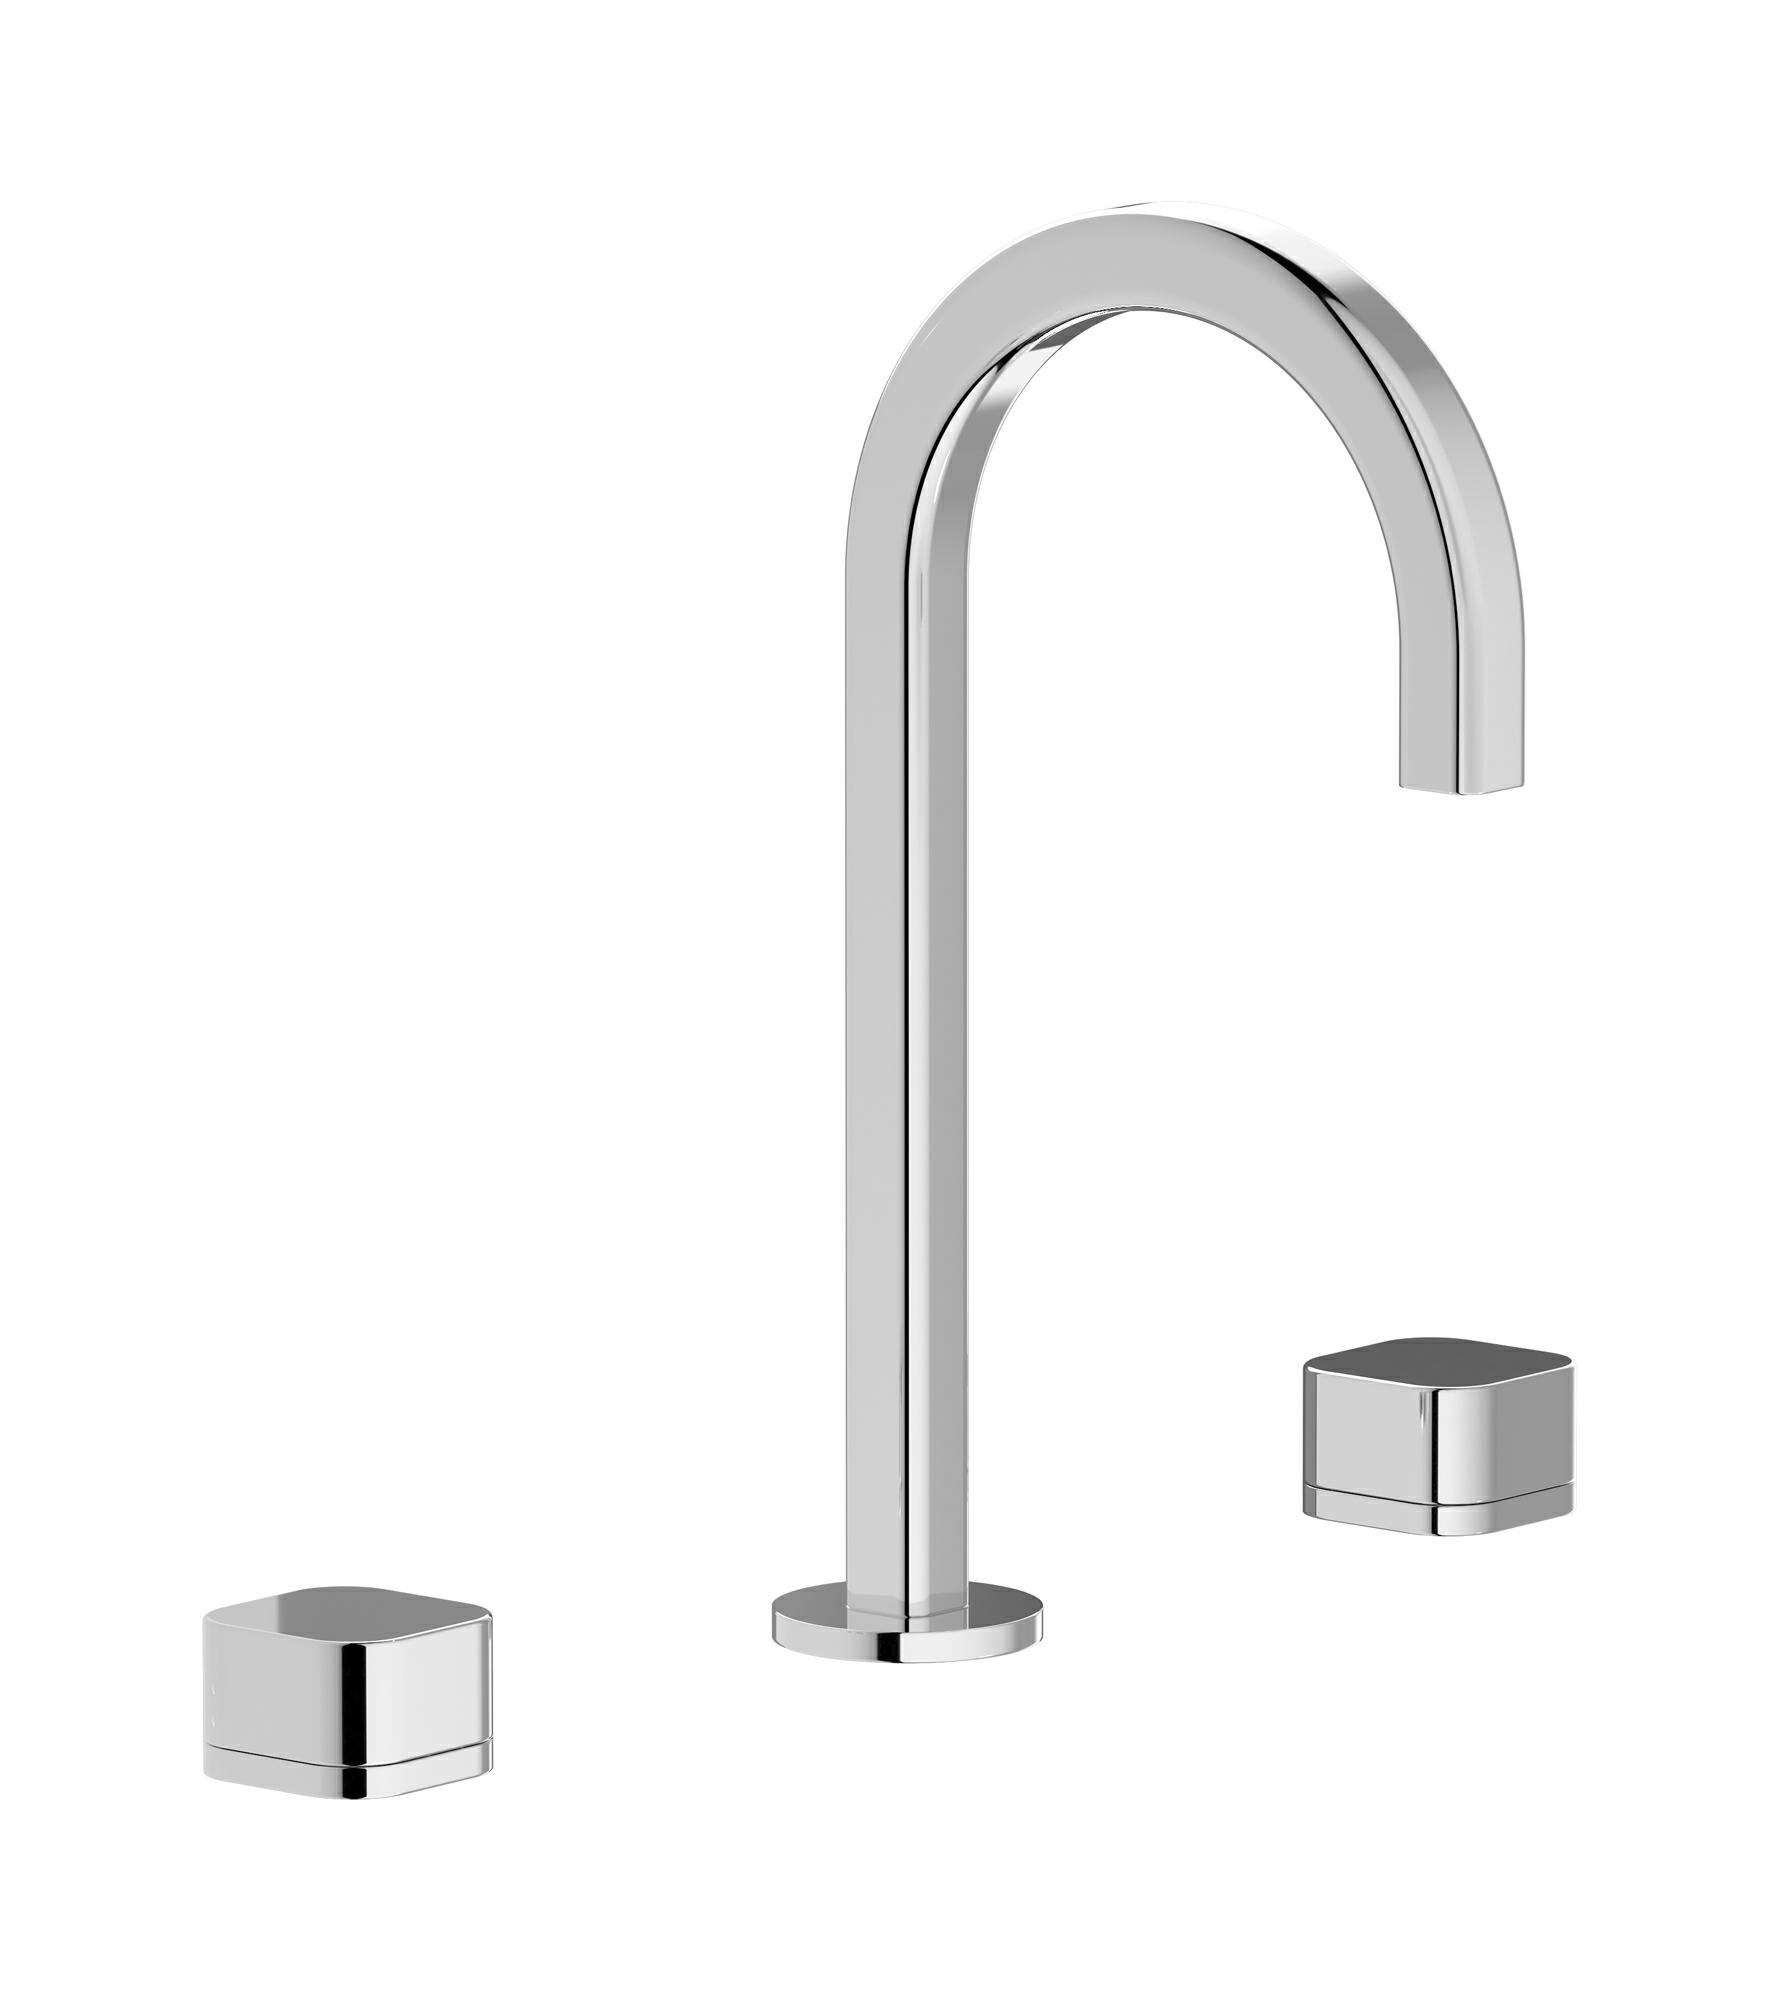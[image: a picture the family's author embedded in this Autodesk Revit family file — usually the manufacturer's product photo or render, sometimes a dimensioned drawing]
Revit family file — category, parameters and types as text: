
# Revit family: EO392_3
name_source: partatom
category: Apparecchi idraulici
units: mm (PartAtom-declared; Revit-internal decimal feet)

## family parameters
Basato su piano di lavoro = No
Condiviso = No
Mantieni orientamento annotazione = No
Numero OmniClass = 23.45.55.17
Punto di calcolo locali = No
Quota connettore circolare = Usa diametro
Sempre verticale = Sì
Taglio con vuoti quando caricato = No
Tipo di parte = Normale
Titolo OmniClass = Mixing Faucets

## types (12) — shared parameters
Cold water inlet = 10 mm  [stored 0.0328084 ft]
Commenti sul tipo = Washbasin
Connessione CW = No
Connessione HW = No
Connessione di scarico = No
Connessione di ventilazione = No
Descrizione = Three hole washbasin complete
Hot water inlet = 10 mm  [stored 0.0328084 ft]
Produttore = IB Rubinetterie S.p.A.
URL = https://www.weareib.it
zero-valued in all types: Prospetto di default

## per-type parameters (varying)
| type | Finishes surface | Immagine tipo | Modello |
| Chrome | IB_Chrome | EO392CC_3.jpg | EO392CC_3 |
| Brushed nickel | IB_Brushed nickel | EO392SS_3.jpg | EO392SS_3 |
| Natural brass | IB_Brass | EO392ON_3.jpg | EO392ON_3 |
| Matt black | IB_matt black | EO392NP_3.jpg | EO392NP_3 |
| Black chrome | IB_Black chrome | EO392CF_3.jpg | EO392CF_3 |
| Brushed black chrome | IB_Brushed black chrome | EO392CS_3.jpg | EO392CS_3 |
| Pale gold | IB_Pale gold | EO392II_3.jpg | EO392II_3 |
| Brushed pale gold | IB_brushed pale gold | EO392IS_3.jpg | EO392IS_3 |
| Rose gold | IB_Rose gold | EO392RS_3.jpg | EO392RS_3 |
| Brushed rose gold | IB_Brushed rose gold | EO392SR_3.jpg | EO392SR_3 |
| Gold | IB_gold | EO392OO_3.jpg | EO392OO_3 |
| Brushed gold | IB_brushed gold | EO392OS_3.jpg | EO392OS_3 |

note: [stored X ft] marks values corroborated as IEEE doubles in the binary element streams (Revit-internal decimal feet)
